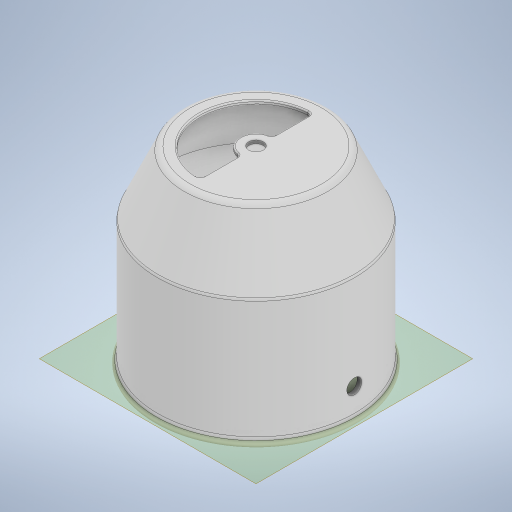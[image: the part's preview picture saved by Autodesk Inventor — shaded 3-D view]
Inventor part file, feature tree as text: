
AUTODESK INVENTOR PART (.ipt)
format: ipt  version: 2024 (Build 280153000, 153)  size: 404,992 bytes
history: native  units: mm
features: sketch x12, extrude x6, fillet x5, plane x5, revolve x1, sweep x1
ambient origin geometry x8: Origin, YZ Plane, XZ Plane, XY Plane, X Axis, Y Axis, Z Axis, Center Point
bodies: Solid1 (feature_tree)
feature tree (30):
  extrude  "Extrusion1"  Depth=5.0mm TaperAngle=0.0deg
  fillet  "Fillet1"  Radius=2.5mm
  extrude  "Extrusion2"  Depth=95.0mm TaperAngle=0.0deg
  plane  "Work Plane1"
  extrude  "Extrusion3"  Depth=110.0mm
  sketch  "Sketch5"  dims[d9=103.0mm d10=3.5mm d11=0.0mm]
  revolve  "Revolution1"  [1 undecoded]
  extrude  "Extrusion4"  TaperAngle=90.0deg  [1 undecoded]
  sketch  "Sketch8"  dims[d19=11.5mm d20=77.5mm]
  plane  "Work Plane2"
  sketch  "Sketch9"  dims[d21=25.0mm d22=10.0mm d23=3.0mm d24=1.0mm]
  fillet  "Fillet2"  Radius=25.0mm
  fillet  "Fillet3"  Radius=88.0mm
  sketch  "Sketch11"  dims[d25=35.0mm]
  extrude  "Extrusion5"  Depth=3.5mm TaperAngle=0.0deg
  sweep  "Sweep1"
  plane  "Work Plane3"
  sketch  "Sketch13"  dims[d27=40.0mm]
  plane  "Work Plane4"
  extrude  "Extrusion7"  Depth=10.0mm
  fillet  "Fillet4"  Radius=3.0mm
  fillet  "Fillet5"  Radius=1.0mm
  plane  "Work Plane5"
  sketch  "Sketch1"  dims[d0=160.0mm d1=5.0mm d2=0.0mm d3=2.5mm]
  sketch  "Sketch2"  dims[d4=148.0mm d5=95.0mm d6=0.0mm]
  sketch  "Sketch3"  dims[d7=50.0mm d8=110.0mm]
  sketch  "Sketch6"  dims[d12=3.5mm d13=90.0deg d14=25.0mm d15=88.0mm]
  sketch  "Sketch7"  dims[d16=88.0mm d17=3.5mm d18=0.0mm]
  sketch  "Sketch12"  dims[d26=35.0mm]
  sketch  "Sketch17"  dims[d28=10.0mm d29=13.75mm d30=26.25mm d31=26.25mm d32=75.0mm d33=8.75mm d34=26.25mm d35=26.25mm d36=26.25mm d37=26.25mm d38=26.25mm d39=10.0mm d40=0.5mm d41=0.0mm d42=0.0mm d43=0.0mm d44=-77.5mm d45=75.0mm d46=11.5mm d47=-175.0mm d64=5.0mm d65=0.0mm d66=2.0mm d67=5.0mm d73=-5.0mm d76=11.7mm d77=1.75mm d78=15.5mm d79=1.75mm d80=9.5mm d54=0.5mm d55=0.872665mm d56=0.5mm d57=0.872665mm d58=0.872665mm d59=0.5mm d60=0.872665mm d68=0.5mm d69=0.872665mm d74=0.0mm d75=0.0mm]
note: 2 required parameter values undecoded (feature->parameter linkage not recoverable at this tier; creation-order binding heuristic only, values carry confidence <= 0.55)